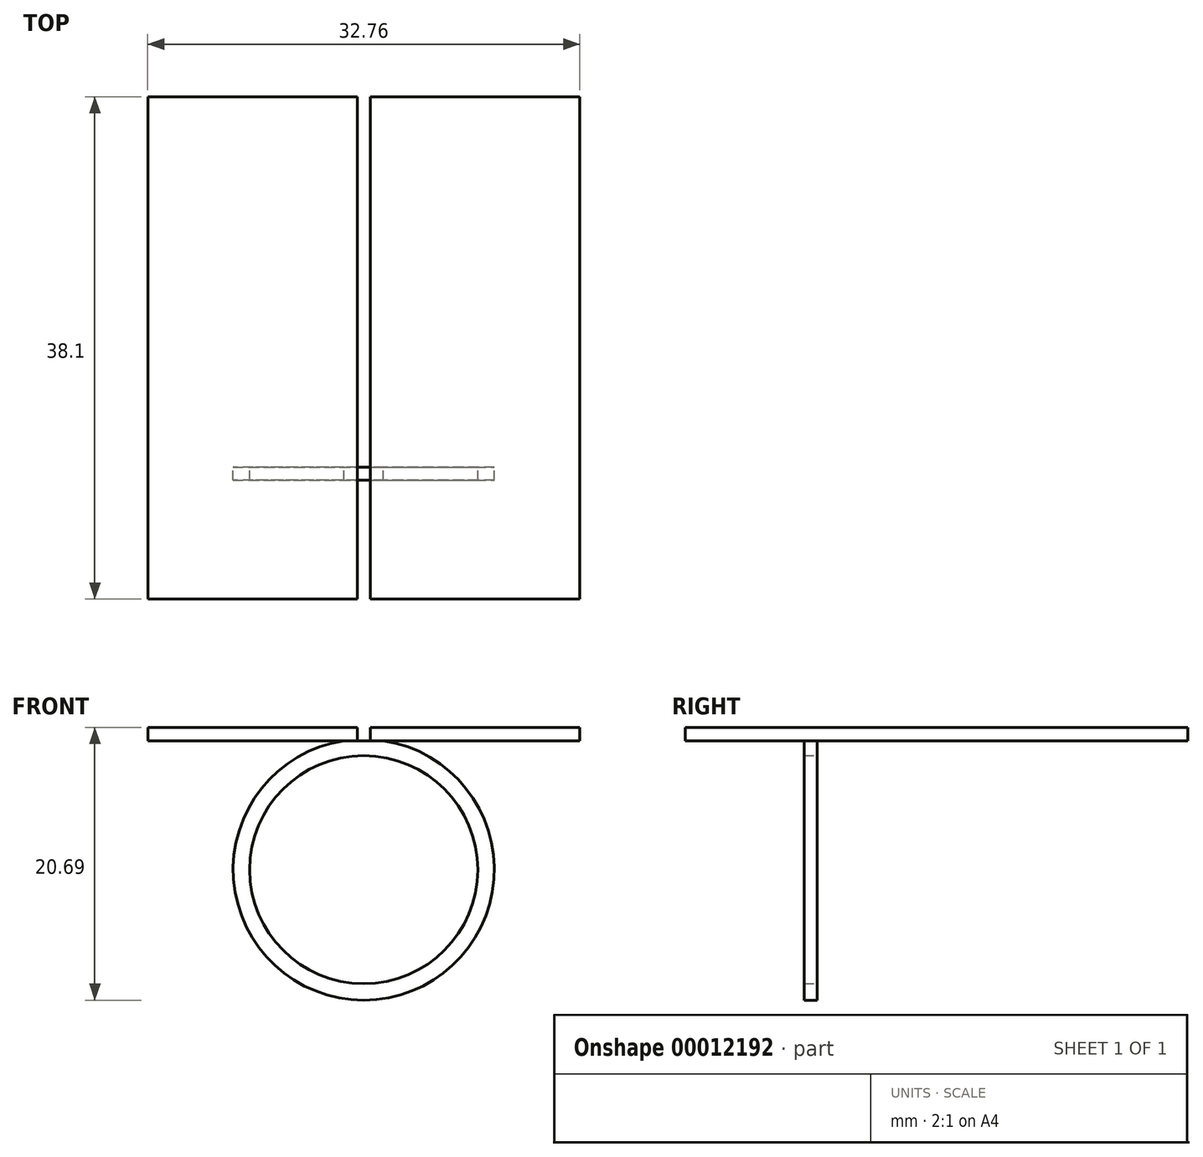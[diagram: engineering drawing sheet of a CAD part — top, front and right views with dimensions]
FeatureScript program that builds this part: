
annotation { "Feature Type Name" : "Feature", "Feature Type Description" : "" }
export const myFeature = defineFeature(function(context is Context, id is Id, definition is map)
    precondition{}
    {
        {
            var Q0;
            Q0=qCreatedBy(makeId("Front.planeOp"),FACE);
            var sketch = newSketch(context, id + "F0", { "sketchPlane" : qUnion([Q0])});
            skCircle(sketch, "E0", {"center": v(0, 0) * mm, "radius": 8.65 * mm});
            skCircle(sketch, "E1", {"center": v(0, 0) * mm, "radius": 9.9 * mm});
            skLineSegment(sketch, "E2", {"start": v(0, 0) * mm, "end": v(1.5, 9.79) * mm});
            skLineSegment(sketch, "E3", {"start": v(1.5, 9.79) * mm, "end": v(0, 9.79) * mm});
            skLineSegment(sketch, "E4", {"start": v(0, 9.79) * mm, "end": v(-1.5, 9.79) * mm});
            skLineSegment(sketch, "E5", {"start": v(-1.5, 9.79) * mm, "end": v(0, 0) * mm});
            skSolve(sketch);
        }
        {
            var Q0;
            {var subQ1=sQuery(id+"F0.wireOp",EDGE,"E0");var subQ5=sQuery(id+"F0.wireOp",EDGE,"E2");var subQ6=makeQuery(id+"F0.imprint","INTERSECT",VERTEX,{"derivedFrom":[subQ1,subQ5]});Q0=makeQuery(id+"F0.imprint","IMPRINT",FACE,{"disambiguationData":[TD([[makeQuery(id+"F0.imprint","IMPRINT",EDGE,{"disambiguationData":[TD([[subQ6,1.0]])],"derivedFrom":subQ1}),-1.0]])]});}
            var Q1;
            {var subQ5=sQuery(id+"F0.wireOp",EDGE,"E3");Q1=makeQuery(id+"F0.imprint","IMPRINT",FACE,{"disambiguationData":[TD([[makeQuery(id+"F0.imprint","IMPRINT",EDGE,{"derivedFrom":subQ5}),1.0]])]});}
            extrude(context, id + "F1", {"entities" : qUnion([Q0, Q1]), "depth" : 1 * mm});
        }
        {
            var Q0;
            {var subQ0=sQuery(id+"F0.wireOp",EDGE,"E3");var subQ1=sQuery(id+"F0.wireOp",EDGE,"E4");Q0=makeQuery(id+"FdzGL64ymaDWjFL_1.boolean.opBoolean","MERGE",FACE,{"derivedFrom":[makeQuery(id+"F1.opExtrude","SWEPT_FACE",FACE,{"disambiguationData":[OSD([subQ0,subQ1])]}),makeQuery(id+"FdzGL64ymaDWjFL_1.opExtrude","SWEPT_FACE",FACE,{"disambiguationData":[OSD([subQ0,subQ1])]})]});}
            var sketch = newSketch(context, id + "F2", { "sketchPlane" : qUnion([Q0])});
            skLineSegment(sketch, "E6.bottom", {"start": v(0.5, -10) * mm, "end": v(16.38, -10) * mm});
            skLineSegment(sketch, "E6.top", {"start": v(0.5, 28.1) * mm, "end": v(16.37, 28.1) * mm});
            skLineSegment(sketch, "E6.left", {"start": v(0.5, -10) * mm, "end": v(0.5, 28.1) * mm});
            skLineSegment(sketch, "E6.right", {"start": v(16.38, -10) * mm, "end": v(16.37, 28.1) * mm});
            skLineSegment(sketch, "E7.bottom", {"start": v(-0.5, -10) * mm, "end": v(-16.37, -10) * mm});
            skLineSegment(sketch, "E7.top", {"start": v(-0.5, 28.1) * mm, "end": v(-16.38, 28.1) * mm});
            skLineSegment(sketch, "E7.left", {"start": v(-0.5, -10) * mm, "end": v(-0.5, 28.1) * mm});
            skLineSegment(sketch, "E7.right", {"start": v(-16.37, -10) * mm, "end": v(-16.38, 28.1) * mm});
            skSolve(sketch);
        }
        {
            var Q0;
            {var subQ11=sQuery(id+"F2.wireOp",EDGE,"E6.bottom");Q0=makeQuery(id+"F2.imprint","IMPRINT",FACE,{"disambiguationData":[TD([[makeQuery(id+"F2.imprint","IMPRINT",EDGE,{"derivedFrom":subQ11}),1.0]])]});}
            var Q1;
            {var subQ11=sQuery(id+"F2.wireOp",EDGE,"E7.bottom");Q1=makeQuery(id+"F2.imprint","IMPRINT",FACE,{"disambiguationData":[TD([[makeQuery(id+"F2.imprint","IMPRINT",EDGE,{"derivedFrom":subQ11}),-1.0]])]});}
            var Q2;
            {var subQ1=sQuery(id+"F0.wireOp",EDGE,"E4");var subQ5=sQuery(id+"F0.wireOp",EDGE,"E1");var subQ6=sQuery(id+"F0.wireOp",EDGE,"E5");var subQ7=makeQuery(id+"FdzGL64ymaDWjFL_1.boolean.opBoolean","MERGE",EDGE,{"derivedFrom":[makeQuery(id+"F1.opExtrude","SWEPT_EDGE",EDGE,{"disambiguationData":[OSD([subQ5,subQ1,subQ6])]}),makeQuery(id+"FdzGL64ymaDWjFL_1.opExtrude","SWEPT_EDGE",EDGE,{"disambiguationData":[OSD([subQ5,subQ1,subQ6])]})]});Q2=makeQuery(id+"F2.imprint","IMPRINT",FACE,{"disambiguationData":[TD([[makeQuery(id+"F2.imprint","IMPRINT",EDGE,{"derivedFrom":subQ7}),-1.0]])]});}
            var Q3;
            {var subQ0=sQuery(id+"F0.wireOp",EDGE,"E3");var subQ5=sQuery(id+"F0.wireOp",EDGE,"E1");var subQ6=sQuery(id+"F0.wireOp",EDGE,"E2");var subQ7=makeQuery(id+"FdzGL64ymaDWjFL_1.boolean.opBoolean","MERGE",EDGE,{"derivedFrom":[makeQuery(id+"F1.opExtrude","SWEPT_EDGE",EDGE,{"disambiguationData":[OSD([subQ5,subQ6,subQ0])]}),makeQuery(id+"FdzGL64ymaDWjFL_1.opExtrude","SWEPT_EDGE",EDGE,{"disambiguationData":[OSD([subQ5,subQ6,subQ0])]})]});Q3=makeQuery(id+"F2.imprint","IMPRINT",FACE,{"disambiguationData":[TD([[makeQuery(id+"F2.imprint","IMPRINT",EDGE,{"derivedFrom":subQ7}),1.0]])]});}
            extrude(context, id + "F3", {"entities" : qUnion([Q0, Q1, Q2, Q3]), "operationType" : NewBodyOperationType.ADD, "depth" : 1 * mm});
        }
    });
